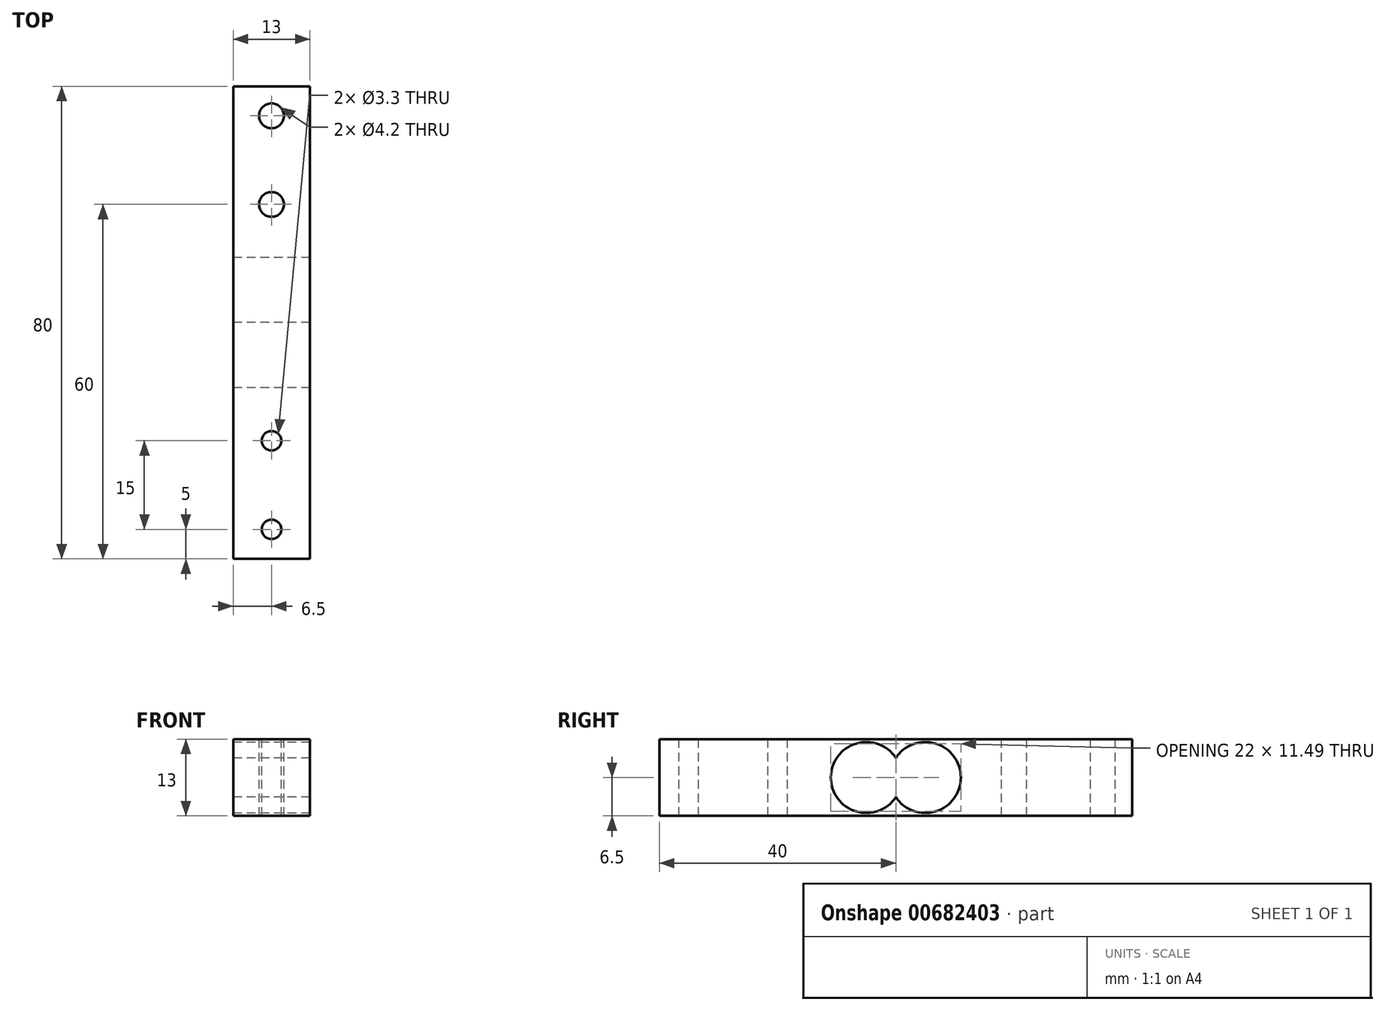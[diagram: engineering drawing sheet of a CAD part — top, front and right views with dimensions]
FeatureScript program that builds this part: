
annotation { "Feature Type Name" : "Feature", "Feature Type Description" : "" }
export const myFeature = defineFeature(function(context is Context, id is Id, definition is map)
    precondition{}
    {
        {
            var Q0;
            Q0=qCreatedBy(makeId("Front.planeOp"),FACE);
            var sketch = newSketch(context, id + "F0", { "sketchPlane" : qUnion([Q0])});
            skLineSegment(sketch, "E0.bottom", {"start": v(6.5, 6.5) * mm, "end": v(-6.5, 6.5) * mm});
            skLineSegment(sketch, "E0.top", {"start": v(6.5, -6.5) * mm, "end": v(-6.5, -6.5) * mm});
            skLineSegment(sketch, "E0.left", {"start": v(6.5, 6.5) * mm, "end": v(6.5, -6.5) * mm});
            skLineSegment(sketch, "E0.right", {"start": v(-6.5, 6.5) * mm, "end": v(-6.5, -6.5) * mm});
            skPoint(sketch, "E0.middle", {"position": v(0, 0) * mm});
            skSolve(sketch);
        }
        {
            var Q0;
            Q0=makeQuery(id+"F0.imprint","IMPRINT",FACE,{"disambiguationData":[TD([[makeQuery(id+"F0.imprint","IMPRINT",EDGE,{"derivedFrom":sQuery(id+"F0.wireOp",EDGE,"E0.bottom")}),1.0]])]});
            extrude(context, id + "F1", {"entities" : qUnion([Q0]), "endBound" : BoundingType.SYMMETRIC, "depth" : 80 * mm, "offsetDistance" : 25 * mm});
        }
        {
            var Q0;
            Q0=qCreatedBy(makeId("Right.planeOp"),FACE);
            var sketch = newSketch(context, id + "F2", { "sketchPlane" : qUnion([Q0])});
            skLineSegment(sketch, "E1", {"start": v(0, 13.76) * mm, "end": v(0, -13.26) * mm, "construction": true});
            skArc(sketch, "E2", {"start": v(0, 3.32) * mm, "mid": v(-11, 0) * mm, "end": v(0, -3.32) * mm});
            skArc(sketch, "E3.MirrorC", {"start": v(0, 3.32) * mm, "mid": v(11, 0) * mm, "end": v(0, -3.32) * mm});
            skSolve(sketch);
        }
        {
            var Q0;
            Q0=makeQuery(id+"F2.imprint","IMPRINT",FACE,{"disambiguationData":[TD([[makeQuery(id+"F2.imprint","IMPRINT",EDGE,{"derivedFrom":sQuery(id+"F2.wireOp",EDGE,"E2")}),1.0]])]});
            extrude(context, id + "F3", {"entities" : qUnion([Q0]), "operationType" : NewBodyOperationType.REMOVE, "endBound" : BoundingType.SYMMETRIC, "depth" : 13 * mm, "offsetDistance" : 25 * mm});
        }
        {
            var Q0;
            Q0=makeQuery(id+"F1.opExtrude","SWEPT_FACE",FACE,{"disambiguationData":[OSD([sQuery(id+"F0.wireOp",EDGE,"E0.bottom")])]});
            var sketch = newSketch(context, id + "F4", { "sketchPlane" : qUnion([Q0])});
            skLineSegment(sketch, "E4", {"start": v(0, -45.07) * mm, "end": v(0, 51.55) * mm, "construction": true});
            skPoint(sketch, "E5", {"position": v(0, -35) * mm});
            skPoint(sketch, "E6", {"position": v(0, -20) * mm});
            skLineSegment(sketch, "E7", {"start": v(-10.08, 0) * mm, "end": v(10.83, 0) * mm, "construction": true});
            skPoint(sketch, "E8.MirrorP", {"position": v(0, 20) * mm});
            skPoint(sketch, "E9.MirrorP", {"position": v(0, 35) * mm});
            skSolve(sketch);
        }
        {
            var Q0;
            Q0=sQuery(id+"F4.wireOp",VERTEX,"E5");
            var Q1;
            Q1=sQuery(id+"F4.wireOp",VERTEX,"E6");
            var Q2;
            Q2=makeQuery(id+"F1.opExtrude","SWEPT_BODY",BODY,{"disambiguationData":[OSD([sQuery(id+"F0.wireOp",EDGE,"E0.bottom"),sQuery(id+"F0.wireOp",EDGE,"E0.top"),sQuery(id+"F0.wireOp",EDGE,"E0.left"),sQuery(id+"F0.wireOp",EDGE,"E0.right")])]});
            hole(context, id + "F5", {"style" : HoleStyle.SIMPLE, "endStyle" : HoleEndStyle.THROUGH, "standardTappedOrClearance" : lookupTablePath({ "standard" : "ISO", "engagement" : "75%", "pitch" : "0.7 mm", "size" : "M4", "type" : "Tapped" }), "standardBlindInLast" : lookupTablePath({ "standard" : "ISO", "engagement" : "75%", "pitch" : "0.7 mm", "size" : "M4", "type" : "Tapped" }), "holeDiameter" : 3.3 * mm, "majorDiameter" : 4 * mm, "showTappedDepth" : true, "isTappedThrough" : true, "tappedDepth" : 17.6 * mm, "tapClearance" : 3, "locations" : qUnion([Q0, Q1]), "scope" : qUnion([Q2])});
        }
        {
            var Q0;
            Q0=sQuery(id+"F4.wireOp",VERTEX,"E8.MirrorP");
            var Q1;
            Q1=sQuery(id+"F4.wireOp",VERTEX,"E9.MirrorP");
            var Q2;
            Q2=makeQuery(id+"F1.opExtrude","SWEPT_BODY",BODY,{"disambiguationData":[OSD([sQuery(id+"F0.wireOp",EDGE,"E0.bottom"),sQuery(id+"F0.wireOp",EDGE,"E0.top"),sQuery(id+"F0.wireOp",EDGE,"E0.left"),sQuery(id+"F0.wireOp",EDGE,"E0.right")])]});
            hole(context, id + "F6", {"style" : HoleStyle.SIMPLE, "endStyle" : HoleEndStyle.THROUGH, "standardTappedOrClearance" : lookupTablePath({ "standard" : "ISO", "engagement" : "75%", "pitch" : "0.8 mm", "size" : "M5", "type" : "Tapped" }), "standardBlindInLast" : lookupTablePath({ "standard" : "ISO", "engagement" : "75%", "pitch" : "0.8 mm", "size" : "M5", "type" : "Tapped" }), "holeDiameter" : 4.2 * mm, "majorDiameter" : 5 * mm, "showTappedDepth" : true, "isTappedThrough" : true, "tappedDepth" : 17.6 * mm, "tapClearance" : 3, "locations" : qUnion([Q0, Q1]), "scope" : qUnion([Q2])});
        }
    });
